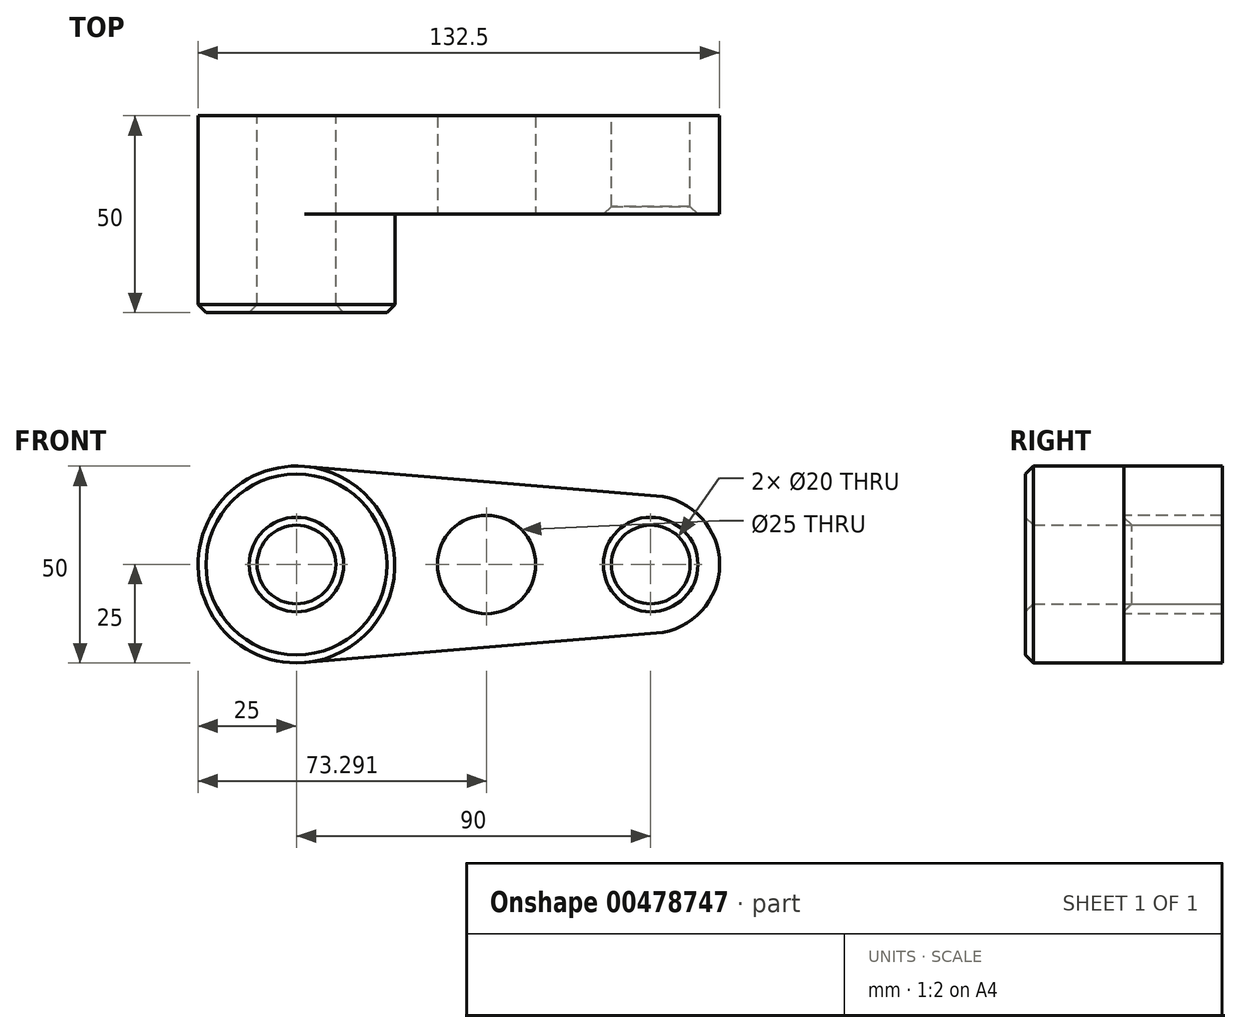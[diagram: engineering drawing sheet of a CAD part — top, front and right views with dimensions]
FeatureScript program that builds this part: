
annotation { "Feature Type Name" : "Feature", "Feature Type Description" : "" }
export const myFeature = defineFeature(function(context is Context, id is Id, definition is map)
    precondition{}
    {
        {
            var Q0;
            Q0=qCreatedBy(makeId("Front.planeOp"),FACE);
            var sketch = newSketch(context, id + "F0", { "sketchPlane" : qUnion([Q0])});
            skCircle(sketch, "E0", {"center": v(0, 0) * mm, "radius": 25 * mm});
            skCircle(sketch, "E1", {"center": v(90, 0) * mm, "radius": 17.5 * mm});
            skLineSegment(sketch, "E2", {"start": v(2.08, 24.91) * mm, "end": v(91.46, 17.44) * mm});
            skLineSegment(sketch, "E3", {"start": v(2.08, -24.91) * mm, "end": v(91.46, -17.44) * mm});
            skCircle(sketch, "E4", {"center": v(0, 0) * mm, "radius": 10 * mm});
            skCircle(sketch, "E5", {"center": v(90, 0) * mm, "radius": 10 * mm});
            skSolve(sketch);
        }
        {
            var Q0;
            Q0=qSketchRegion(id+"F0",true);
            extrude(context, id + "F1", {"entities" : qUnion([Q0]), "depth" : 25 * mm});
        }
        {
            var Q0;
            Q0=makeQuery(id+"F0.imprint","IMPRINT",FACE,{"disambiguationData":[TD([[makeQuery(id+"F0.imprint","IMPRINT",EDGE,{"derivedFrom":sQuery(id+"F0.wireOp",EDGE,"E4")}),-1.0]])]});
            extrude(context, id + "F2", {"entities" : qUnion([Q0]), "operationType" : NewBodyOperationType.ADD, "depth" : 50 * mm});
        }
        {
            var Q0;
            Q0=makeQuery(id+"F2.opExtrude","CAP_EDGE",EDGE,{"disambiguationData":[OSD([sQuery(id+"F0.wireOp",EDGE,"E0")])],"isStart":false});
            var Q1;
            Q1=makeQuery(id+"F2.opExtrude","CAP_EDGE",EDGE,{"disambiguationData":[OSD([sQuery(id+"F0.wireOp",EDGE,"E4")])],"isStart":false});
            var Q2;
            Q2=makeQuery(id+"F1.opExtrude","CAP_EDGE",EDGE,{"disambiguationData":[OSD([sQuery(id+"F0.wireOp",EDGE,"E5")])],"isStart":false});
            chamfer(context, id + "F3", {"entities" : qUnion([Q0, Q1, Q2]), "width" : 2 * mm, "tangentPropagation" : true});
        }
        {
            var Q0;
            Q0=qCreatedBy(makeId("Right.planeOp"),FACE);
            var sketch = newSketch(context, id + "F4", { "sketchPlane" : qUnion([Q0])});
            skLineSegment(sketch, "E6.bottom", {"start": v(24.06, 44) * mm, "end": v(-55.94, 44) * mm});
            skLineSegment(sketch, "E6.top", {"start": v(24.06, 14) * mm, "end": v(-55.94, 14) * mm});
            skLineSegment(sketch, "E6.left", {"start": v(24.06, 44) * mm, "end": v(24.06, 14) * mm});
            skLineSegment(sketch, "E6.right", {"start": v(-55.94, 44) * mm, "end": v(-55.94, 14) * mm});
            skSolve(sketch);
        }
        {
            var Q0;
            Q0=makeQuery(id+"F1.opExtrude","CAP_FACE",FACE,{"disambiguationData":[OSD([sQuery(id+"F0.wireOp",EDGE,"E0"),sQuery(id+"F0.wireOp",EDGE,"E1"),sQuery(id+"F0.wireOp",EDGE,"E2"),sQuery(id+"F0.wireOp",EDGE,"E3"),sQuery(id+"F0.wireOp",EDGE,"E4"),sQuery(id+"F0.wireOp",EDGE,"E5")])],"isStart":false});
            var sketch = newSketch(context, id + "F5", { "sketchPlane" : qUnion([Q0])});
            skCircle(sketch, "E7", {"center": v(48.3, 0) * mm, "radius": 12.5 * mm});
            skSolve(sketch);
        }
        {
            var Q0;
            Q0 = qSketchRegion(id + "F5", true);
            extrude(context, id + "F6", {"entities" : qUnion([Q0]), "operationType" : NewBodyOperationType.REMOVE, "endBound" : BoundingType.THROUGH_ALL, "oppositeDirection" : true, "depth" : 25 * mm});
        }
    });
